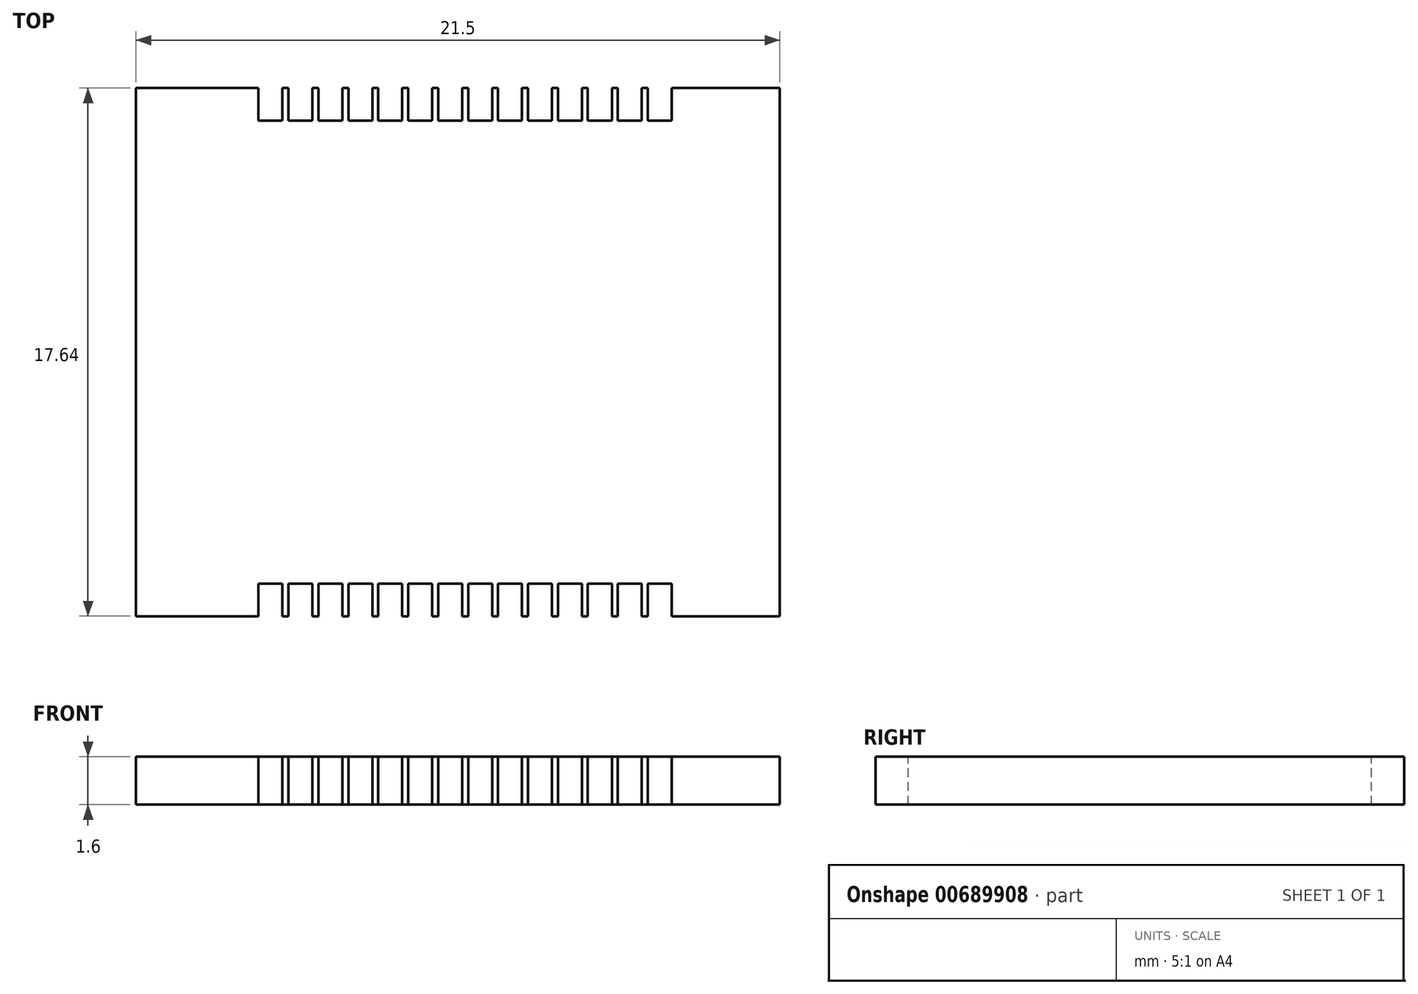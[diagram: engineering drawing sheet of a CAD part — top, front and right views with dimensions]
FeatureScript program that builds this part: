
annotation { "Feature Type Name" : "Feature", "Feature Type Description" : "" }
export const myFeature = defineFeature(function(context is Context, id is Id, definition is map)
    precondition{}
    {
        {
            var Q0;
            Q0=qCreatedBy(makeId("Top.planeOp"),FACE);
            var sketch = newSketch(context, id + "F0", { "sketchPlane" : qUnion([Q0])});
            skLineSegment(sketch, "E0.bottom", {"start": v(10.75, -8.82) * mm, "end": v(-10.75, -8.82) * mm});
            skLineSegment(sketch, "E0.top", {"start": v(10.75, 8.82) * mm, "end": v(-10.75, 8.82) * mm});
            skLineSegment(sketch, "E0.left", {"start": v(10.75, -8.82) * mm, "end": v(10.75, 8.83) * mm});
            skLineSegment(sketch, "E0.right", {"start": v(-10.75, -8.82) * mm, "end": v(-10.75, 8.83) * mm});
            skPoint(sketch, "E0.middle", {"position": v(0, 0) * mm});
            skSolve(sketch);
        }
        {
            var Q0;
            Q0 = qSketchRegion(id + "F0", true);
            extrude(context, id + "F1", {"entities" : qUnion([Q0]), "depth" : 1.6 * mm, "offsetDistance" : 25 * mm});
        }
        {
            var Q0;
            Q0=makeQuery(id+"F1.opExtrude","CAP_FACE",FACE,{"disambiguationData":[OSD([sQuery(id+"F0.wireOp",EDGE,"E0.bottom"),sQuery(id+"F0.wireOp",EDGE,"E0.top"),sQuery(id+"F0.wireOp",EDGE,"E0.left"),sQuery(id+"F0.wireOp",EDGE,"E0.right")])],"isStart":false});
            cPlane(context, id + "F2", {"entities" : qUnion([Q0]), "cplaneType" : CPlaneType.OFFSET, "offset" : (35e-3) * mm, "width" : 150 * mm, "height" : 150 * mm});
        }
        {
            var Q0;
            Q0=qCreatedBy(id+"F2.planeOp",FACE);
            var sketch = newSketch(context, id + "F3", { "sketchPlane" : qUnion([Q0])});
            skLineSegment(sketch, "E1.bottom", {"start": v(-6.66, 8.82) * mm, "end": v(-5.86, 8.82) * mm});
            skLineSegment(sketch, "E1.top", {"start": v(-6.66, 7.73) * mm, "end": v(-5.86, 7.73) * mm});
            skLineSegment(sketch, "E1.left", {"start": v(-6.66, 8.82) * mm, "end": v(-6.66, 7.73) * mm});
            skLineSegment(sketch, "E1.right", {"start": v(-5.86, 8.82) * mm, "end": v(-5.86, 7.73) * mm});
            skLineSegment(sketch, "E2", {"start": v(-6.26, 8.82) * mm, "end": v(-6.26, 7.73) * mm, "construction": true});
            skLineSegment(sketch, "E3.1.0.0", {"start": v(-5.26, 8.82) * mm, "end": v(-5.26, 7.73) * mm, "construction": true});
            skLineSegment(sketch, "E3.1.0.1", {"start": v(-5.66, 8.82) * mm, "end": v(-5.66, 7.73) * mm});
            skLineSegment(sketch, "E3.1.0.2", {"start": v(-5.66, 7.73) * mm, "end": v(-4.86, 7.73) * mm});
            skLineSegment(sketch, "E3.1.0.3", {"start": v(-5.66, 8.82) * mm, "end": v(-4.86, 8.82) * mm});
            skLineSegment(sketch, "E3.1.0.4", {"start": v(-4.86, 8.82) * mm, "end": v(-4.86, 7.73) * mm});
            skLineSegment(sketch, "E3.2.0.0", {"start": v(-4.26, 8.82) * mm, "end": v(-4.26, 7.73) * mm, "construction": true});
            skLineSegment(sketch, "E3.2.0.1", {"start": v(-4.66, 8.82) * mm, "end": v(-4.66, 7.73) * mm});
            skLineSegment(sketch, "E3.2.0.2", {"start": v(-4.66, 7.73) * mm, "end": v(-3.86, 7.73) * mm});
            skLineSegment(sketch, "E3.2.0.3", {"start": v(-4.66, 8.82) * mm, "end": v(-3.86, 8.82) * mm});
            skLineSegment(sketch, "E3.2.0.4", {"start": v(-3.86, 8.82) * mm, "end": v(-3.86, 7.73) * mm});
            skLineSegment(sketch, "E3.3.0.0", {"start": v(-3.26, 8.82) * mm, "end": v(-3.26, 7.73) * mm, "construction": true});
            skLineSegment(sketch, "E3.3.0.1", {"start": v(-3.66, 8.82) * mm, "end": v(-3.66, 7.73) * mm});
            skLineSegment(sketch, "E3.3.0.2", {"start": v(-3.66, 7.73) * mm, "end": v(-2.86, 7.73) * mm});
            skLineSegment(sketch, "E3.3.0.3", {"start": v(-3.66, 8.82) * mm, "end": v(-2.86, 8.82) * mm});
            skLineSegment(sketch, "E3.3.0.4", {"start": v(-2.86, 8.82) * mm, "end": v(-2.86, 7.73) * mm});
            skLineSegment(sketch, "E3.4.0.0", {"start": v(-2.26, 8.82) * mm, "end": v(-2.26, 7.73) * mm, "construction": true});
            skLineSegment(sketch, "E3.4.0.1", {"start": v(-2.66, 8.82) * mm, "end": v(-2.66, 7.73) * mm});
            skLineSegment(sketch, "E3.4.0.2", {"start": v(-2.66, 7.73) * mm, "end": v(-1.86, 7.73) * mm});
            skLineSegment(sketch, "E3.4.0.3", {"start": v(-2.66, 8.82) * mm, "end": v(-1.86, 8.82) * mm});
            skLineSegment(sketch, "E3.4.0.4", {"start": v(-1.86, 8.82) * mm, "end": v(-1.86, 7.73) * mm});
            skLineSegment(sketch, "E3.5.0.0", {"start": v(-1.26, 8.82) * mm, "end": v(-1.26, 7.73) * mm, "construction": true});
            skLineSegment(sketch, "E3.5.0.1", {"start": v(-1.66, 8.82) * mm, "end": v(-1.66, 7.73) * mm});
            skLineSegment(sketch, "E3.5.0.2", {"start": v(-1.66, 7.73) * mm, "end": v(-0.86, 7.73) * mm});
            skLineSegment(sketch, "E3.5.0.3", {"start": v(-1.66, 8.82) * mm, "end": v(-0.86, 8.82) * mm});
            skLineSegment(sketch, "E3.5.0.4", {"start": v(-0.86, 8.82) * mm, "end": v(-0.86, 7.73) * mm});
            skLineSegment(sketch, "E3.6.0.0", {"start": v(-0.26, 8.82) * mm, "end": v(-0.26, 7.73) * mm, "construction": true});
            skLineSegment(sketch, "E3.6.0.1", {"start": v(-0.66, 8.82) * mm, "end": v(-0.66, 7.73) * mm});
            skLineSegment(sketch, "E3.6.0.2", {"start": v(-0.66, 7.73) * mm, "end": v(0.14, 7.73) * mm});
            skLineSegment(sketch, "E3.6.0.3", {"start": v(-0.66, 8.82) * mm, "end": v(0.14, 8.82) * mm});
            skLineSegment(sketch, "E3.6.0.4", {"start": v(0.14, 8.82) * mm, "end": v(0.14, 7.73) * mm});
            skLineSegment(sketch, "E3.7.0.0", {"start": v(0.74, 8.82) * mm, "end": v(0.74, 7.73) * mm, "construction": true});
            skLineSegment(sketch, "E3.7.0.1", {"start": v(0.34, 8.82) * mm, "end": v(0.34, 7.73) * mm});
            skLineSegment(sketch, "E3.7.0.2", {"start": v(0.34, 7.73) * mm, "end": v(1.14, 7.73) * mm});
            skLineSegment(sketch, "E3.7.0.3", {"start": v(0.34, 8.82) * mm, "end": v(1.14, 8.82) * mm});
            skLineSegment(sketch, "E3.7.0.4", {"start": v(1.14, 8.82) * mm, "end": v(1.14, 7.73) * mm});
            skLineSegment(sketch, "E3.8.0.0", {"start": v(1.74, 8.82) * mm, "end": v(1.74, 7.73) * mm, "construction": true});
            skLineSegment(sketch, "E3.8.0.1", {"start": v(1.34, 8.82) * mm, "end": v(1.34, 7.73) * mm});
            skLineSegment(sketch, "E3.8.0.2", {"start": v(1.34, 7.73) * mm, "end": v(2.14, 7.73) * mm});
            skLineSegment(sketch, "E3.8.0.3", {"start": v(1.34, 8.82) * mm, "end": v(2.14, 8.82) * mm});
            skLineSegment(sketch, "E3.8.0.4", {"start": v(2.14, 8.82) * mm, "end": v(2.14, 7.73) * mm});
            skLineSegment(sketch, "E3.9.0.0", {"start": v(2.74, 8.82) * mm, "end": v(2.74, 7.73) * mm, "construction": true});
            skLineSegment(sketch, "E3.9.0.1", {"start": v(2.34, 8.82) * mm, "end": v(2.34, 7.73) * mm});
            skLineSegment(sketch, "E3.9.0.2", {"start": v(2.34, 7.73) * mm, "end": v(3.14, 7.73) * mm});
            skLineSegment(sketch, "E3.9.0.3", {"start": v(2.34, 8.82) * mm, "end": v(3.14, 8.82) * mm});
            skLineSegment(sketch, "E3.9.0.4", {"start": v(3.14, 8.82) * mm, "end": v(3.14, 7.73) * mm});
            skLineSegment(sketch, "E3.10.0.0", {"start": v(3.74, 8.82) * mm, "end": v(3.74, 7.73) * mm, "construction": true});
            skLineSegment(sketch, "E3.10.0.1", {"start": v(3.34, 8.82) * mm, "end": v(3.34, 7.73) * mm});
            skLineSegment(sketch, "E3.10.0.2", {"start": v(3.34, 7.73) * mm, "end": v(4.14, 7.73) * mm});
            skLineSegment(sketch, "E3.10.0.3", {"start": v(3.34, 8.82) * mm, "end": v(4.14, 8.82) * mm});
            skLineSegment(sketch, "E3.10.0.4", {"start": v(4.14, 8.82) * mm, "end": v(4.14, 7.73) * mm});
            skLineSegment(sketch, "E3.11.0.0", {"start": v(4.74, 8.82) * mm, "end": v(4.74, 7.73) * mm, "construction": true});
            skLineSegment(sketch, "E3.11.0.1", {"start": v(4.34, 8.82) * mm, "end": v(4.34, 7.73) * mm});
            skLineSegment(sketch, "E3.11.0.2", {"start": v(4.34, 7.73) * mm, "end": v(5.14, 7.73) * mm});
            skLineSegment(sketch, "E3.11.0.3", {"start": v(4.34, 8.82) * mm, "end": v(5.14, 8.82) * mm});
            skLineSegment(sketch, "E3.11.0.4", {"start": v(5.14, 8.82) * mm, "end": v(5.14, 7.73) * mm});
            skLineSegment(sketch, "E3.12.0.0", {"start": v(5.74, 8.82) * mm, "end": v(5.74, 7.73) * mm, "construction": true});
            skLineSegment(sketch, "E3.12.0.1", {"start": v(5.34, 8.82) * mm, "end": v(5.34, 7.73) * mm});
            skLineSegment(sketch, "E3.12.0.2", {"start": v(5.34, 7.73) * mm, "end": v(6.14, 7.73) * mm});
            skLineSegment(sketch, "E3.12.0.3", {"start": v(5.34, 8.82) * mm, "end": v(6.14, 8.82) * mm});
            skLineSegment(sketch, "E3.12.0.4", {"start": v(6.14, 8.82) * mm, "end": v(6.14, 7.73) * mm});
            skLineSegment(sketch, "E3.13.0.0", {"start": v(6.74, 8.82) * mm, "end": v(6.74, 7.73) * mm, "construction": true});
            skLineSegment(sketch, "E3.13.0.1", {"start": v(6.34, 8.82) * mm, "end": v(6.34, 7.73) * mm});
            skLineSegment(sketch, "E3.13.0.2", {"start": v(6.34, 7.73) * mm, "end": v(7.14, 7.73) * mm});
            skLineSegment(sketch, "E3.13.0.3", {"start": v(6.34, 8.82) * mm, "end": v(7.14, 8.82) * mm});
            skLineSegment(sketch, "E3.13.0.4", {"start": v(7.14, 8.82) * mm, "end": v(7.14, 7.73) * mm});
            skLineSegment(sketch, "E3.direction1", {"start": v(-6.66, 7.73) * mm, "end": v(-5.66, 7.73) * mm, "construction": true});
            skLineSegment(sketch, "E4.MirrorCS", {"start": v(-6.66, -7.73) * mm, "end": v(-5.86, -7.73) * mm});
            skLineSegment(sketch, "E5.MirrorCS", {"start": v(3.34, -7.73) * mm, "end": v(4.14, -7.73) * mm});
            skLineSegment(sketch, "E6.MirrorCS", {"start": v(6.34, -8.82) * mm, "end": v(7.14, -8.82) * mm});
            skLineSegment(sketch, "E7.MirrorCS", {"start": v(-1.66, -7.73) * mm, "end": v(-0.86, -7.73) * mm});
            skLineSegment(sketch, "E8.MirrorCS", {"start": v(1.34, -8.82) * mm, "end": v(2.14, -8.82) * mm});
            skLineSegment(sketch, "E9.MirrorCS", {"start": v(6.34, -7.73) * mm, "end": v(7.14, -7.73) * mm});
            skLineSegment(sketch, "E10.MirrorCS", {"start": v(1.34, -7.73) * mm, "end": v(2.14, -7.73) * mm});
            skLineSegment(sketch, "E11.MirrorCS", {"start": v(4.34, -8.82) * mm, "end": v(5.14, -8.82) * mm});
            skLineSegment(sketch, "E12.MirrorCS", {"start": v(-4.66, -7.73) * mm, "end": v(-3.86, -7.73) * mm});
            skLineSegment(sketch, "E13.MirrorCS", {"start": v(-5.66, -8.82) * mm, "end": v(-4.86, -8.82) * mm});
            skLineSegment(sketch, "E14.MirrorCS", {"start": v(-5.66, -7.73) * mm, "end": v(-4.86, -7.73) * mm});
            skLineSegment(sketch, "E15.MirrorCS", {"start": v(-1.66, -8.82) * mm, "end": v(-0.86, -8.82) * mm});
            skLineSegment(sketch, "E16.MirrorCS", {"start": v(5.34, -7.73) * mm, "end": v(6.14, -7.73) * mm});
            skLineSegment(sketch, "E17.MirrorCS", {"start": v(3.34, -8.82) * mm, "end": v(4.14, -8.82) * mm});
            skLineSegment(sketch, "E18.MirrorCS", {"start": v(0.34, -7.73) * mm, "end": v(1.14, -7.73) * mm});
            skLineSegment(sketch, "E19.MirrorCS", {"start": v(-3.66, -7.73) * mm, "end": v(-2.86, -7.73) * mm});
            skLineSegment(sketch, "E20.MirrorCS", {"start": v(-0.66, -8.82) * mm, "end": v(0.14, -8.82) * mm});
            skLineSegment(sketch, "E21.MirrorCS", {"start": v(4.34, -7.73) * mm, "end": v(5.14, -7.73) * mm});
            skLineSegment(sketch, "E22.MirrorCS", {"start": v(-2.66, -7.73) * mm, "end": v(-1.86, -7.73) * mm});
            skLineSegment(sketch, "E23.MirrorCS", {"start": v(-6.66, -7.73) * mm, "end": v(-5.66, -7.73) * mm, "construction": true});
            skLineSegment(sketch, "E24.MirrorCS", {"start": v(5.34, -8.82) * mm, "end": v(6.14, -8.82) * mm});
            skLineSegment(sketch, "E25.MirrorCS", {"start": v(-4.66, -8.82) * mm, "end": v(-3.86, -8.82) * mm});
            skLineSegment(sketch, "E26.MirrorCS", {"start": v(-3.66, -8.82) * mm, "end": v(-2.86, -8.82) * mm});
            skLineSegment(sketch, "E27.MirrorCS", {"start": v(-6.66, -8.82) * mm, "end": v(-5.86, -8.82) * mm});
            skLineSegment(sketch, "E28.MirrorCS", {"start": v(2.34, -8.82) * mm, "end": v(3.14, -8.82) * mm});
            skLineSegment(sketch, "E29.MirrorCS", {"start": v(-2.66, -8.82) * mm, "end": v(-1.86, -8.82) * mm});
            skLineSegment(sketch, "E30.MirrorCS", {"start": v(2.34, -7.73) * mm, "end": v(3.14, -7.73) * mm});
            skLineSegment(sketch, "E31.MirrorCS", {"start": v(0.34, -8.82) * mm, "end": v(1.14, -8.82) * mm});
            skLineSegment(sketch, "E32.MirrorCS", {"start": v(-0.66, -7.73) * mm, "end": v(0.14, -7.73) * mm});
            skLineSegment(sketch, "E33.MirrorCS", {"start": v(-0.86, -8.82) * mm, "end": v(-0.86, -7.73) * mm});
            skLineSegment(sketch, "E34.MirrorCS", {"start": v(0.34, -8.82) * mm, "end": v(0.34, -7.73) * mm});
            skLineSegment(sketch, "E35.MirrorCS", {"start": v(2.74, -8.82) * mm, "end": v(2.74, -7.73) * mm, "construction": true});
            skLineSegment(sketch, "E36.MirrorCS", {"start": v(5.34, -8.82) * mm, "end": v(5.34, -7.73) * mm});
            skLineSegment(sketch, "E37.MirrorCS", {"start": v(-2.26, -8.82) * mm, "end": v(-2.26, -7.73) * mm, "construction": true});
            skLineSegment(sketch, "E38.MirrorCS", {"start": v(5.14, -8.82) * mm, "end": v(5.14, -7.73) * mm});
            skLineSegment(sketch, "E39.MirrorCS", {"start": v(0.74, -8.82) * mm, "end": v(0.74, -7.73) * mm, "construction": true});
            skLineSegment(sketch, "E40.MirrorCS", {"start": v(3.34, -8.82) * mm, "end": v(3.34, -7.73) * mm});
            skLineSegment(sketch, "E41.MirrorCS", {"start": v(-2.86, -8.82) * mm, "end": v(-2.86, -7.73) * mm});
            skLineSegment(sketch, "E42.MirrorCS", {"start": v(-1.66, -8.82) * mm, "end": v(-1.66, -7.73) * mm});
            skLineSegment(sketch, "E43.MirrorCS", {"start": v(-4.66, -8.82) * mm, "end": v(-4.66, -7.73) * mm});
            skLineSegment(sketch, "E44.MirrorCS", {"start": v(-4.26, -8.82) * mm, "end": v(-4.26, -7.73) * mm, "construction": true});
            skLineSegment(sketch, "E45.MirrorCS", {"start": v(-4.86, -8.82) * mm, "end": v(-4.86, -7.73) * mm});
            skLineSegment(sketch, "E46.MirrorCS", {"start": v(-5.66, -8.82) * mm, "end": v(-5.66, -7.73) * mm});
            skLineSegment(sketch, "E47.MirrorCS", {"start": v(-5.26, -8.82) * mm, "end": v(-5.26, -7.73) * mm, "construction": true});
            skLineSegment(sketch, "E48.MirrorCS", {"start": v(-6.26, -8.82) * mm, "end": v(-6.26, -7.73) * mm, "construction": true});
            skLineSegment(sketch, "E49.MirrorCS", {"start": v(-5.86, -8.82) * mm, "end": v(-5.86, -7.73) * mm});
            skLineSegment(sketch, "E50.MirrorCS", {"start": v(-6.66, -8.82) * mm, "end": v(-6.66, -7.73) * mm});
            skLineSegment(sketch, "E51.MirrorCS", {"start": v(-3.66, -8.82) * mm, "end": v(-3.66, -7.73) * mm});
            skLineSegment(sketch, "E52.MirrorCS", {"start": v(-2.66, -8.82) * mm, "end": v(-2.66, -7.73) * mm});
            skLineSegment(sketch, "E53.MirrorCS", {"start": v(4.34, -8.82) * mm, "end": v(4.34, -7.73) * mm});
            skLineSegment(sketch, "E54.MirrorCS", {"start": v(1.74, -8.82) * mm, "end": v(1.74, -7.73) * mm, "construction": true});
            skLineSegment(sketch, "E55.MirrorCS", {"start": v(2.14, -8.82) * mm, "end": v(2.14, -7.73) * mm});
            skLineSegment(sketch, "E56.MirrorCS", {"start": v(-1.86, -8.82) * mm, "end": v(-1.86, -7.73) * mm});
            skLineSegment(sketch, "E57.MirrorCS", {"start": v(5.74, -8.82) * mm, "end": v(5.74, -7.73) * mm, "construction": true});
            skLineSegment(sketch, "E58.MirrorCS", {"start": v(7.14, -8.82) * mm, "end": v(7.14, -7.73) * mm});
            skLineSegment(sketch, "E59.MirrorCS", {"start": v(2.34, -8.82) * mm, "end": v(2.34, -7.73) * mm});
            skLineSegment(sketch, "E60.MirrorCS", {"start": v(-0.26, -8.82) * mm, "end": v(-0.26, -7.73) * mm, "construction": true});
            skLineSegment(sketch, "E61.MirrorCS", {"start": v(6.74, -8.82) * mm, "end": v(6.74, -7.73) * mm, "construction": true});
            skLineSegment(sketch, "E62.MirrorCS", {"start": v(3.14, -8.82) * mm, "end": v(3.14, -7.73) * mm});
            skLineSegment(sketch, "E63.MirrorCS", {"start": v(4.14, -8.82) * mm, "end": v(4.14, -7.73) * mm});
            skLineSegment(sketch, "E64.MirrorCS", {"start": v(1.34, -8.82) * mm, "end": v(1.34, -7.73) * mm});
            skLineSegment(sketch, "E65.MirrorCS", {"start": v(-1.26, -8.82) * mm, "end": v(-1.26, -7.73) * mm, "construction": true});
            skLineSegment(sketch, "E66.MirrorCS", {"start": v(-3.86, -8.82) * mm, "end": v(-3.86, -7.73) * mm});
            skLineSegment(sketch, "E67.MirrorCS", {"start": v(-3.26, -8.82) * mm, "end": v(-3.26, -7.73) * mm, "construction": true});
            skLineSegment(sketch, "E68.MirrorCS", {"start": v(0.14, -8.82) * mm, "end": v(0.14, -7.73) * mm});
            skLineSegment(sketch, "E69.MirrorCS", {"start": v(3.74, -8.82) * mm, "end": v(3.74, -7.73) * mm, "construction": true});
            skLineSegment(sketch, "E70.MirrorCS", {"start": v(1.14, -8.82) * mm, "end": v(1.14, -7.73) * mm});
            skLineSegment(sketch, "E71.MirrorCS", {"start": v(4.74, -8.82) * mm, "end": v(4.74, -7.73) * mm, "construction": true});
            skLineSegment(sketch, "E72.MirrorCS", {"start": v(6.14, -8.82) * mm, "end": v(6.14, -7.73) * mm});
            skLineSegment(sketch, "E73.MirrorCS", {"start": v(-0.66, -8.82) * mm, "end": v(-0.66, -7.73) * mm});
            skLineSegment(sketch, "E74.MirrorCS", {"start": v(6.34, -8.82) * mm, "end": v(6.34, -7.73) * mm});
            skSolve(sketch);
        }
        {
            var Q0;
            Q0 = qSketchRegion(id + "F3", true);
            extrude(context, id + "F4", {"entities" : qUnion([Q0]), "operationType" : NewBodyOperationType.REMOVE, "oppositeDirection" : true, "depth" : 25 * mm, "offsetDistance" : 25 * mm});
        }
    });
